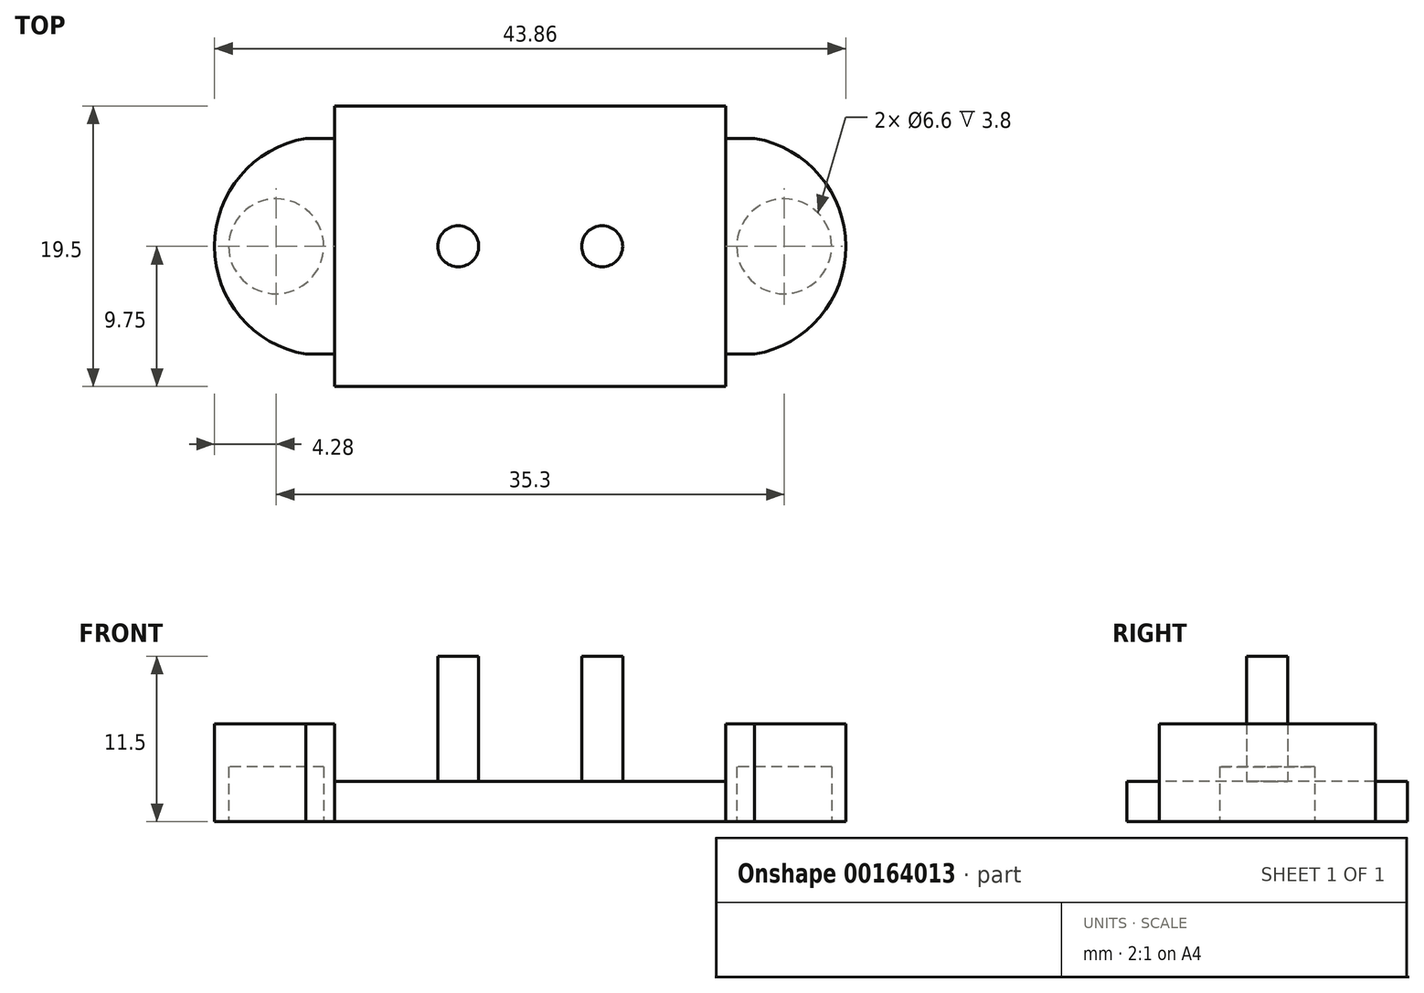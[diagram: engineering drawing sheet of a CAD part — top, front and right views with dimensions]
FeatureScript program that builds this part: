
annotation { "Feature Type Name" : "Feature", "Feature Type Description" : "" }
export const myFeature = defineFeature(function(context is Context, id is Id, definition is map)
    precondition{}
    {
        {
            var Q0;
            Q0=qCreatedBy(makeId("Top.planeOp"),FACE);
            var sketch = newSketch(context, id + "F0", { "sketchPlane" : qUnion([Q0])});
            skLineSegment(sketch, "E0.bottom", {"start": v(13.6, 9.75) * mm, "end": v(-13.6, 9.75) * mm});
            skLineSegment(sketch, "E0.top", {"start": v(13.6, -9.75) * mm, "end": v(-13.6, -9.75) * mm});
            skLineSegment(sketch, "E0.left", {"start": v(13.6, 9.75) * mm, "end": v(13.6, 7.5) * mm});
            skLineSegment(sketch, "E0.right", {"start": v(-13.6, 9.75) * mm, "end": v(-13.6, 7.5) * mm});
            skPoint(sketch, "E0.middle", {"position": v(0, 0) * mm});
            skLineSegment(sketch, "E1.trimOffspring", {"start": v(13.6, -7.5) * mm, "end": v(13.6, -9.75) * mm});
            skLineSegment(sketch, "E2.trimOffspring", {"start": v(-13.6, -7.5) * mm, "end": v(-13.6, -9.75) * mm});
            skPoint(sketch, "E3.center.orphan", {"position": v(13.6, 0) * mm});
            skLineSegment(sketch, "E4", {"start": v(13.6, -7.5) * mm, "end": v(15.6, -7.5) * mm});
            skLineSegment(sketch, "E5.MirrorCS", {"start": v(13.6, 7.5) * mm, "end": v(15.6, 7.5) * mm});
            skLineSegment(sketch, "E6.MirrorCS", {"start": v(-13.6, -7.5) * mm, "end": v(-15.6, -7.5) * mm});
            skLineSegment(sketch, "E7.MirrorCS", {"start": v(-13.6, 7.5) * mm, "end": v(-15.6, 7.5) * mm});
            skArc(sketch, "E8", {"start": v(15.6, -7.5) * mm, "mid": v(21.93, 0) * mm, "end": v(15.6, 7.5) * mm});
            skArc(sketch, "E9.MirrorCS", {"start": v(-15.6, -7.5) * mm, "mid": v(-21.93, 0) * mm, "end": v(-15.6, 7.5) * mm});
            skSolve(sketch);
        }
        {
            var Q0;
            Q0 = qSketchRegion(id + "F0", true);
            extrude(context, id + "F1", {"entities" : qUnion([Q0]), "depth" : 6.8 * mm});
        }
        {
            var Q0;
            Q0=makeQuery(id+"F1.opExtrude","CAP_FACE",FACE,{"disambiguationData":[OSD([sQuery(id+"F0.wireOp",EDGE,"E0.bottom"),sQuery(id+"F0.wireOp",EDGE,"E0.top"),sQuery(id+"F0.wireOp",EDGE,"E0.left"),sQuery(id+"F0.wireOp",EDGE,"E0.right"),sQuery(id+"F0.wireOp",EDGE,"E3"),sQuery(id+"F0.wireOp",EDGE,"E1.trimOffspring"),sQuery(id+"F0.wireOp",EDGE,"91c77974-853e-4d96-a227-c5c103ff6c240.MirrorCS"),sQuery(id+"F0.wireOp",EDGE,"E2.trimOffspring")])],"isStart":false});
            var sketch = newSketch(context, id + "F2", { "sketchPlane" : qUnion([Q0])});
            skLineSegment(sketch, "E10.bottom", {"start": v(13.6, 9.75) * mm, "end": v(-13.6, 9.75) * mm});
            skLineSegment(sketch, "E10.top", {"start": v(13.6, -9.75) * mm, "end": v(-13.6, -9.75) * mm});
            skLineSegment(sketch, "E10.left", {"start": v(13.6, 9.75) * mm, "end": v(13.6, -9.75) * mm});
            skLineSegment(sketch, "E10.right", {"start": v(-13.6, 9.75) * mm, "end": v(-13.6, -9.75) * mm});
            skPoint(sketch, "E10.middle", {"position": v(0, 0) * mm});
            skSolve(sketch);
        }
        {
            var Q0;
            Q0 = qSketchRegion(id + "F2", true);
            extrude(context, id + "F3", {"entities" : qUnion([Q0]), "operationType" : NewBodyOperationType.REMOVE, "oppositeDirection" : true, "depth" : 4 * mm});
        }
        {
            var Q0;
            Q0=qCreatedBy(makeId("Top.planeOp"),FACE);
            var sketch = newSketch(context, id + "F4", { "sketchPlane" : qUnion([Q0])});
            skCircle(sketch, "E11", {"center": v(17.65, 0) * mm, "radius": 3.3 * mm});
            skCircle(sketch, "E12.MirrorC", {"center": v(-17.65, 0) * mm, "radius": 3.3 * mm});
            skSolve(sketch);
        }
        {
            var Q0;
            Q0 = qSketchRegion(id + "F4", true);
            extrude(context, id + "F5", {"entities" : qUnion([Q0]), "operationType" : NewBodyOperationType.REMOVE, "depth" : 3.8 * mm});
        }
        {
            var Q0;
            Q0=makeQuery(id+"F3.boolean.opBoolean","COPY",FACE,{"derivedFrom":makeQuery(id+"F3.opExtrude","CAP_FACE",FACE,{"disambiguationData":[OSD([sQuery(id+"F2.wireOp",EDGE,"E10.bottom"),sQuery(id+"F2.wireOp",EDGE,"E10.top"),sQuery(id+"F2.wireOp",EDGE,"E10.left"),sQuery(id+"F2.wireOp",EDGE,"E10.right")])],"isStart":false})});
            var sketch = newSketch(context, id + "F6", { "sketchPlane" : qUnion([Q0])});
            skCircle(sketch, "E13", {"center": v(5, 0) * mm, "radius": 1.43 * mm});
            skCircle(sketch, "E14.MirrorC", {"center": v(-5, 0) * mm, "radius": 1.43 * mm});
            skSolve(sketch);
        }
        {
            var Q0;
            Q0 = qSketchRegion(id + "F6", true);
            extrude(context, id + "F7", {"entities" : qUnion([Q0]), "operationType" : NewBodyOperationType.ADD, "depth" : 8.7 * mm});
        }
    });
